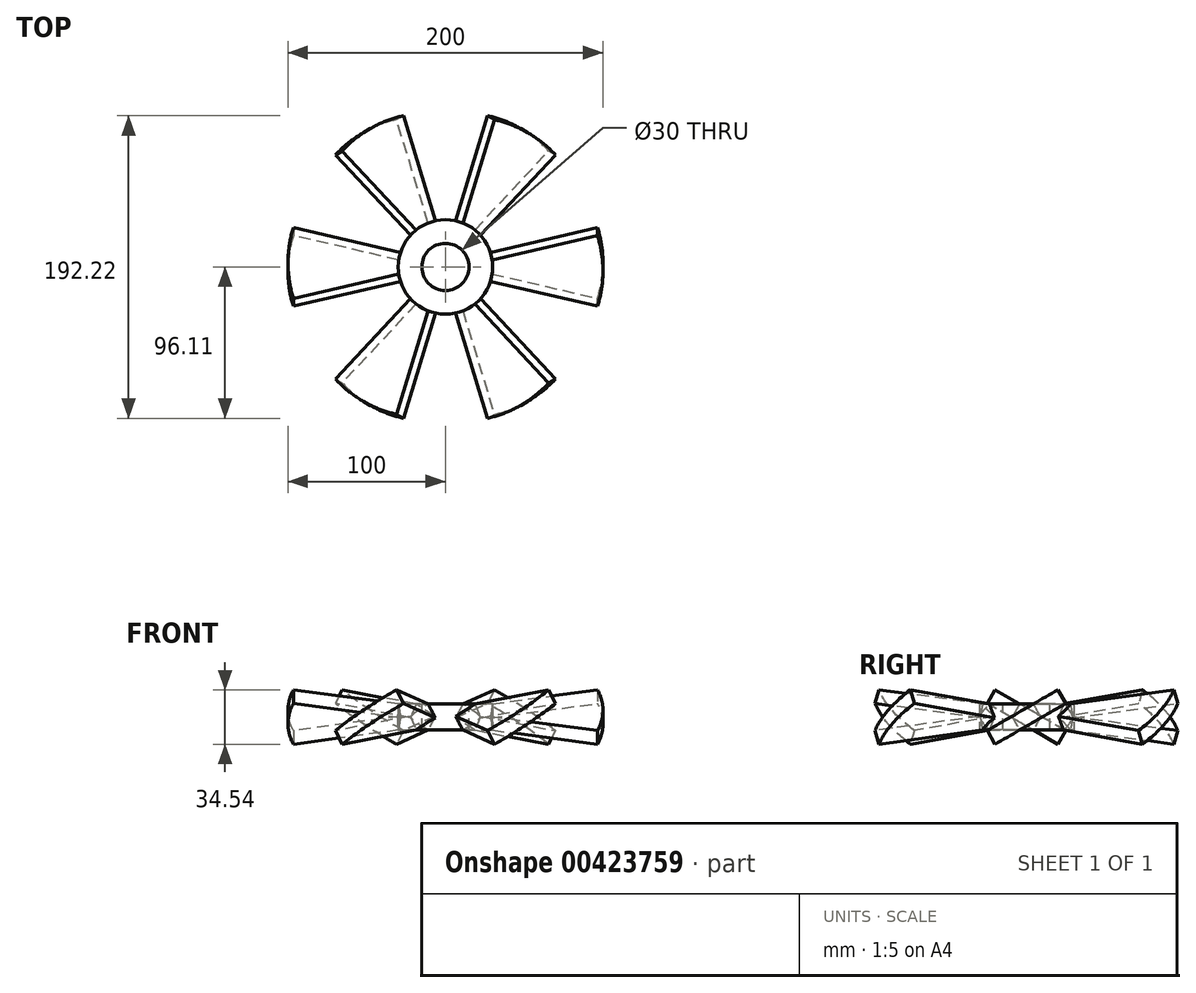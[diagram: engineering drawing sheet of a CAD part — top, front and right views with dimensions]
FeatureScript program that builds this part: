
annotation { "Feature Type Name" : "Feature", "Feature Type Description" : "" }
export const myFeature = defineFeature(function(context is Context, id is Id, definition is map)
    precondition{}
    {
        {
            var Q0;
            Q0=qCreatedBy(makeId("Top.planeOp"),FACE);
            var sketch = newSketch(context, id + "F0", { "sketchPlane" : qUnion([Q0])});
            skArc(sketch, "E0", {"start": v(96.6, -25.88) * mm, "mid": v(100, 0) * mm, "end": v(96.6, 25.88) * mm});
            skLineSegment(sketch, "E1", {"start": v(0, 0) * mm, "end": v(96.6, 25.88) * mm});
            skLineSegment(sketch, "E2.MirrorCS", {"start": v(0, 0) * mm, "end": v(96.6, -25.88) * mm});
            skSolve(sketch);
        }
        {
            var Q0;
            Q0=makeQuery(id+"F0.imprint","IMPRINT",FACE,{"disambiguationData":[TD([[makeQuery(id+"F0.imprint","IMPRINT",EDGE,{"derivedFrom":sQuery(id+"F0.wireOp",EDGE,"E0")}),1.0]])]});
            extrude(context, id + "F1", {"entities" : qUnion([Q0]), "endBound" : BoundingType.SYMMETRIC, "depth" : 10 * mm});
        }
        {
            var Q0;
            Q0=qCreatedBy(makeId("Top.planeOp"),FACE);
            var sketch = newSketch(context, id + "F2", { "sketchPlane" : qUnion([Q0])});
            skLineSegment(sketch, "E3", {"start": v(0, 0) * mm, "end": v(156.33, 0) * mm});
            skSolve(sketch);
        }
        {
            var Q0;
            Q0=makeQuery(id+"F1.opExtrude","SWEPT_BODY",BODY,{"disambiguationData":[OSD([sQuery(id+"F0.wireOp",EDGE,"E0"),sQuery(id+"F0.wireOp",EDGE,"E1"),sQuery(id+"F0.wireOp",EDGE,"E2.MirrorCS")])]});
            var Q1;
            Q1=sQuery(id+"F2.wireOp",EDGE,"E3");
            transform(context, id + "F3", {"entities" : qUnion([Q0]), "transformType" : TransformType.ROTATION, "transformAxis" : qUnion([Q1]), "angle" : 30 * degree, "makeCopy" : false});
        }
        {
            var Q0;
            Q0=qCreatedBy(makeId("Right.planeOp"),FACE);
            var sketch = newSketch(context, id + "F4", { "sketchPlane" : qUnion([Q0])});
            skLineSegment(sketch, "E4", {"start": v(0, 0) * mm, "end": v(0, 83.34) * mm});
            skSolve(sketch);
        }
        {
            var Q0;
            Q0=makeQuery(id+"F1.opExtrude","SWEPT_BODY",BODY,{"disambiguationData":[OSD([sQuery(id+"F0.wireOp",EDGE,"E0"),sQuery(id+"F0.wireOp",EDGE,"E1"),sQuery(id+"F0.wireOp",EDGE,"E2.MirrorCS")])]});
            var Q1;
            Q1=sQuery(id+"F4.wireOp",EDGE,"E4");
            circularPattern(context, id + "F5", {"entities" : qUnion([Q0]), "axis" : qUnion([Q1]), "angle" : 360 * degree, "instanceCount" : 6, "equalSpace" : true});
        }
        {
            var Q0;
            Q0=qCreatedBy(makeId("Top.planeOp"),FACE);
            var sketch = newSketch(context, id + "F6", { "sketchPlane" : qUnion([Q0])});
            skCircle(sketch, "E5", {"center": v(0, 0) * mm, "radius": 30 * mm});
            skSolve(sketch);
        }
        {
            var Q0;
            Q0 = qSketchRegion(id + "F6", true);
            extrude(context, id + "F7", {"entities" : qUnion([Q0]), "operationType" : NewBodyOperationType.REMOVE, "endBound" : BoundingType.SYMMETRIC, "oppositeDirection" : true, "depth" : 25 * mm});
        }
        {
            var Q0;
            Q0 = qSketchRegion(id + "F6", true);
            var Q1;
            {var subQ0=sQuery(id+"F0.wireOp",EDGE,"E1");Q1=makeQuery(id+"F7.boolean.opBoolean","INTERSECT",VERTEX,{"derivedFrom":[makeQuery(id+"F5.opPattern","COPY",FACE,{"derivedFrom":makeQuery(id+"F1.opExtrude","CAP_FACE",FACE,{"disambiguationData":[OSD([sQuery(id+"F0.wireOp",EDGE,"E0"),subQ0,sQuery(id+"F0.wireOp",EDGE,"E2.MirrorCS")])],"isStart":false}),"instanceName":"2"}),makeQuery(id+"F5.opPattern","COPY",FACE,{"derivedFrom":makeQuery(id+"F1.opExtrude","SWEPT_FACE",FACE,{"disambiguationData":[OSD([subQ0])]}),"instanceName":"2"}),makeQuery(id+"F7.opExtrude","SWEPT_FACE",FACE,{"disambiguationData":[OSD([sQuery(id+"F6.wireOp",EDGE,"E5")])]})]});}
            var Q2;
            {var subQ0=sQuery(id+"F0.wireOp",EDGE,"E2.MirrorCS");Q2=makeQuery(id+"F7.boolean.opBoolean","INTERSECT",VERTEX,{"derivedFrom":[makeQuery(id+"F5.opPattern","COPY",FACE,{"derivedFrom":makeQuery(id+"F1.opExtrude","CAP_FACE",FACE,{"disambiguationData":[OSD([sQuery(id+"F0.wireOp",EDGE,"E0"),sQuery(id+"F0.wireOp",EDGE,"E1"),subQ0])],"isStart":true}),"instanceName":"5"}),makeQuery(id+"F5.opPattern","COPY",FACE,{"derivedFrom":makeQuery(id+"F1.opExtrude","SWEPT_FACE",FACE,{"disambiguationData":[OSD([subQ0])]}),"instanceName":"5"}),makeQuery(id+"F7.opExtrude","SWEPT_FACE",FACE,{"disambiguationData":[OSD([sQuery(id+"F6.wireOp",EDGE,"E5")])]})]});}
            extrude(context, id + "F8", {"entities" : qUnion([Q0]), "endBound" : BoundingType.UP_TO_VERTEX, "endBoundEntityVertex" : qUnion([Q1]), "depth" : 25 * mm, "hasSecondDirection" : true, "secondDirectionBound" : SecondDirectionBoundingType.UP_TO_VERTEX, "secondDirectionOppositeDirection" : true, "secondDirectionBoundEntityVertex" : qUnion([Q2]), "secondDirectionDepth" : 25 * mm});
        }
        {
            var Q0;
            Q0=makeQuery(id+"F8.opExtrude","CAP_FACE",FACE,{"disambiguationData":[OSD([sQuery(id+"F6.wireOp",EDGE,"E5")])],"isStart":false});
            var sketch = newSketch(context, id + "F9", { "sketchPlane" : qUnion([Q0])});
            skCircle(sketch, "E6", {"center": v(0, 0) * mm, "radius": 15 * mm});
            skSolve(sketch);
        }
        {
            var Q0;
            Q0 = qSketchRegion(id + "F9", true);
            extrude(context, id + "F10", {"entities" : qUnion([Q0]), "operationType" : NewBodyOperationType.REMOVE, "oppositeDirection" : true, "depth" : 25 * mm});
        }
    });
